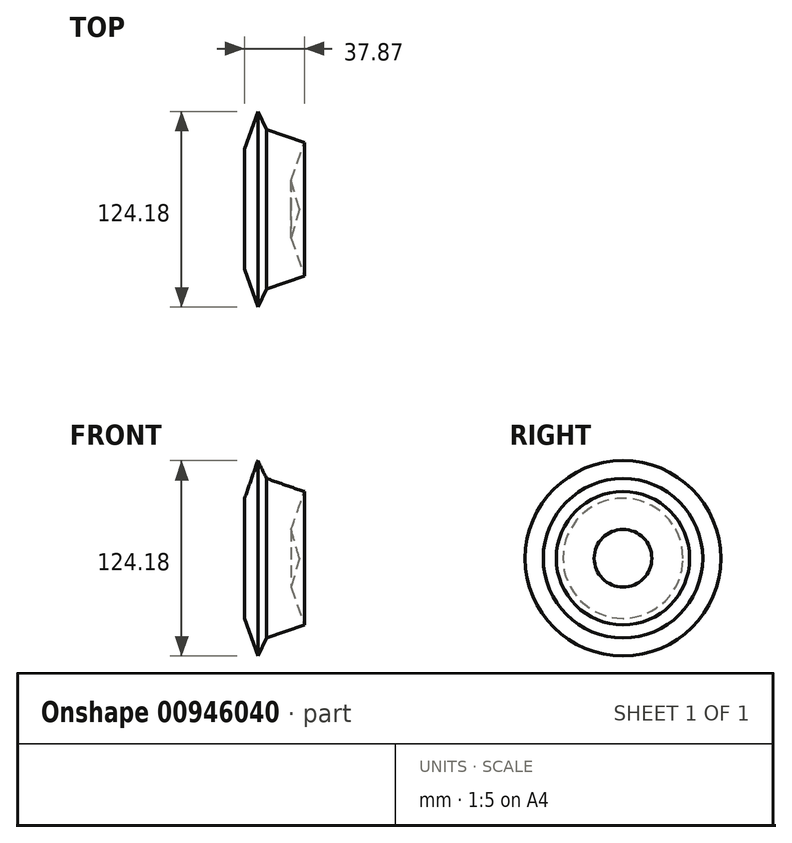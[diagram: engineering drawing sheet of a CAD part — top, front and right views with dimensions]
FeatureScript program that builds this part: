
annotation { "Feature Type Name" : "Feature", "Feature Type Description" : "" }
export const myFeature = defineFeature(function(context is Context, id is Id, definition is map)
    precondition{}
    {
        {
            var Q0;
            Q0=qCreatedBy(makeId("Top.planeOp"),FACE);
            var sketch = newSketch(context, id + "F0", { "sketchPlane" : qUnion([Q0])});
            skLineSegment(sketch, "E0", {"start": v(0, 0) * mm, "end": v(0, 38.1) * mm, "construction": true});
            skLineSegment(sketch, "E1", {"start": v(0, 0) * mm, "end": v(34.72, 0) * mm});
            skLineSegment(sketch, "E2", {"start": v(34.72, 0) * mm, "end": v(29.52, 18.33) * mm});
            skLineSegment(sketch, "E3", {"start": v(29.52, 18.33) * mm, "end": v(37.87, 42.32) * mm});
            skLineSegment(sketch, "E4", {"start": v(37.87, 42.32) * mm, "end": v(13.87, 50.66) * mm});
            skLineSegment(sketch, "E5", {"start": v(13.87, 50.66) * mm, "end": v(8.34, 62.1) * mm});
            skLineSegment(sketch, "E6", {"start": v(8.34, 62.1) * mm, "end": v(0, 38.1) * mm});
            skLineSegment(sketch, "E7", {"start": v(0, 38.1) * mm, "end": v(0, 0) * mm});
            skSolve(sketch);
        }
        {
            var Q0;
            Q0=makeQuery(id+"F0.imprint","IMPRINT",FACE,{"disambiguationData":[TD([[makeQuery(id+"F0.imprint","IMPRINT",EDGE,{"derivedFrom":sQuery(id+"F0.wireOp",EDGE,"E1")}),1.0]])]});
            var Q1;
            Q1=sQuery(id+"F0.wireOp",EDGE,"E1");
            revolve(context, id + "F1", {"surfaceOperationType" : NewSurfaceOperationType.NEW, "entities" : qUnion([Q0]), "axis" : qUnion([Q1]), "revolveType" : RevolveType.FULL});
        }
    });
